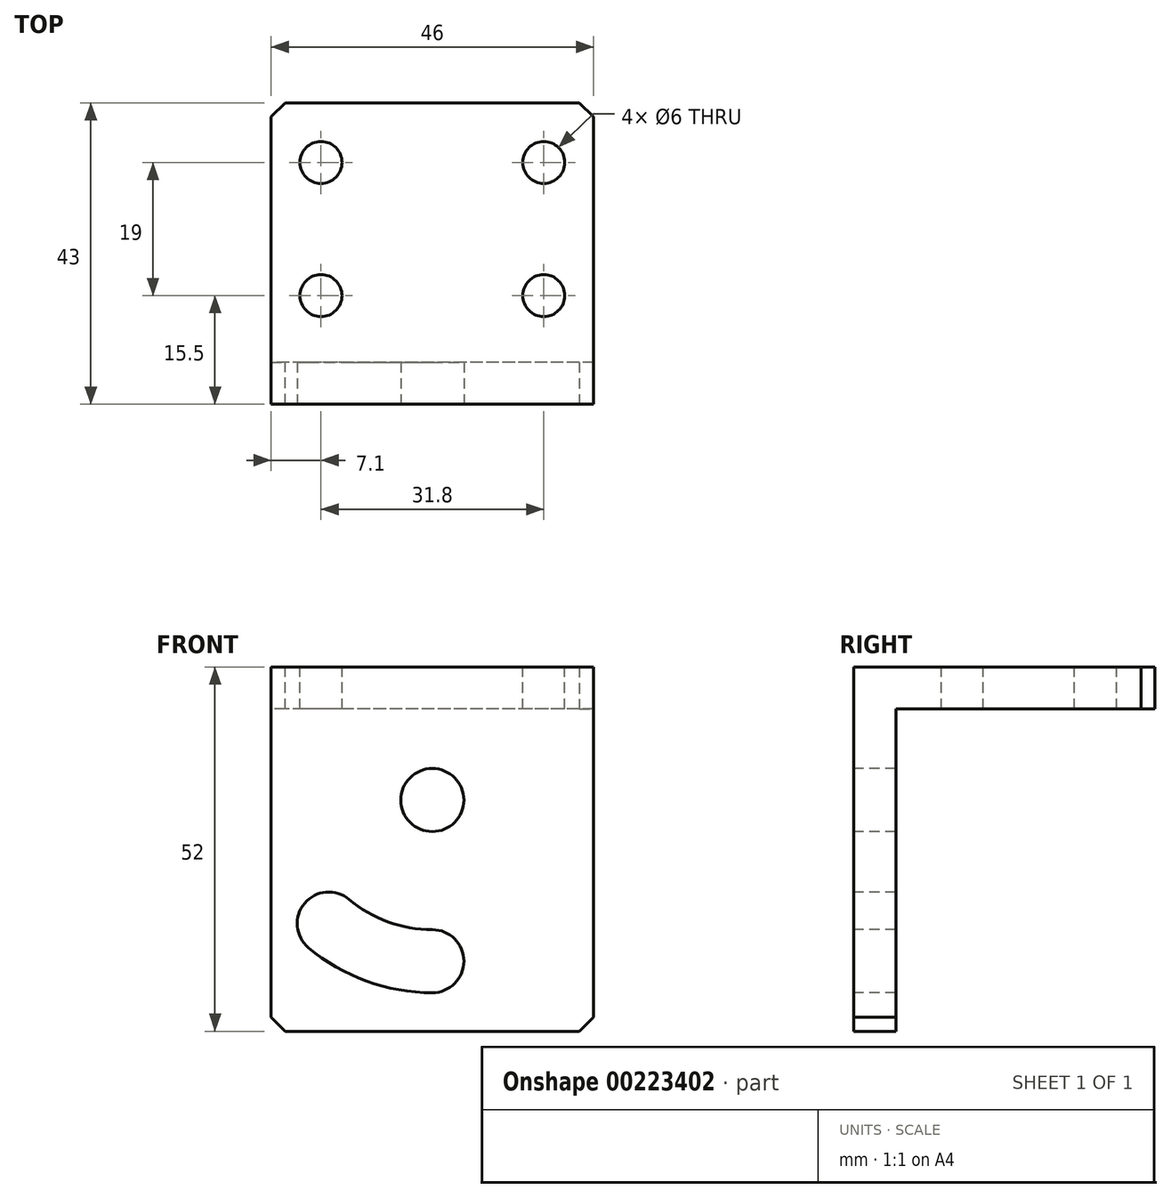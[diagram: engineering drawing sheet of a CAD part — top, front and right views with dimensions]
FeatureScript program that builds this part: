
annotation { "Feature Type Name" : "Feature", "Feature Type Description" : "" }
export const myFeature = defineFeature(function(context is Context, id is Id, definition is map)
    precondition{}
    {
        {
            var Q0;
            Q0=qCreatedBy(makeId("Right.planeOp"),FACE);
            var sketch = newSketch(context, id + "F0", { "sketchPlane" : qUnion([Q0])});
            skLineSegment(sketch, "E0", {"start": v(0, 0) * mm, "end": v(0, -52) * mm});
            skLineSegment(sketch, "E1", {"start": v(0, -52) * mm, "end": v(6, -52) * mm});
            skLineSegment(sketch, "E2", {"start": v(6, -52) * mm, "end": v(6, -6) * mm});
            skLineSegment(sketch, "E3", {"start": v(6, -6) * mm, "end": v(43, -6) * mm});
            skLineSegment(sketch, "E4", {"start": v(43, -6) * mm, "end": v(43, 0) * mm});
            skLineSegment(sketch, "E5", {"start": v(43, 0) * mm, "end": v(0, 0) * mm});
            skSolve(sketch);
        }
        {
            var Q0;
            Q0 = qSketchRegion(id + "F0", true);
            extrude(context, id + "F1", {"entities" : qUnion([Q0]), "depth" : 46 * mm});
        }
        {
            var Q0;
            Q0=qCreatedBy(makeId("Top.planeOp"),FACE);
            var sketch = newSketch(context, id + "F2", { "sketchPlane" : qUnion([Q0])});
            skLineSegment(sketch, "E6", {"start": v(23, -4.49) * mm, "end": v(23, 57.42) * mm});
            skCircle(sketch, "E7", {"center": v(38.9, 15.5) * mm, "radius": 3 * mm});
            skCircle(sketch, "E8", {"center": v(38.9, 34.5) * mm, "radius": 3 * mm});
            skCircle(sketch, "E9.MirrorC", {"center": v(7.1, 15.5) * mm, "radius": 3 * mm});
            skCircle(sketch, "E10.MirrorC", {"center": v(7.1, 34.5) * mm, "radius": 3 * mm});
            skSolve(sketch);
        }
        {
            var Q0;
            Q0 = qSketchRegion(id + "F2", true);
            extrude(context, id + "F3", {"entities" : qUnion([Q0]), "operationType" : NewBodyOperationType.REMOVE, "oppositeDirection" : true, "depth" : 25 * mm});
        }
        {
            var Q0;
            Q0=makeQuery(id+"F1.opExtrude","SWEPT_FACE",FACE,{"disambiguationData":[OSD([sQuery(id+"F0.wireOp",EDGE,"E0")])]});
            var sketch = newSketch(context, id + "F4", { "sketchPlane" : qUnion([Q0])});
            skCircle(sketch, "E11", {"center": v(23, -19) * mm, "radius": 4.5 * mm});
            skArc(sketch, "E12", {"start": v(11.1, -33.17) * mm, "mid": v(16.67, -36.38) * mm, "end": v(23, -37.5) * mm});
            skArc(sketch, "E13", {"start": v(5.32, -40.07) * mm, "mid": v(13.6, -44.84) * mm, "end": v(23, -46.5) * mm});
            skArc(sketch, "E14", {"start": v(23, -46.5) * mm, "mid": v(27.5, -42) * mm, "end": v(23, -37.5) * mm});
            skArc(sketch, "E15", {"start": v(11.1, -33.17) * mm, "mid": v(4.77, -33.73) * mm, "end": v(5.32, -40.07) * mm});
            skSolve(sketch);
        }
        {
            var Q0;
            Q0 = qSketchRegion(id + "F4", true);
            extrude(context, id + "F5", {"entities" : qUnion([Q0]), "operationType" : NewBodyOperationType.REMOVE, "oppositeDirection" : true, "depth" : 25 * mm});
        }
        {
            var Q0;
            Q0=makeQuery(id+"F1.opExtrude","CAP_EDGE",EDGE,{"disambiguationData":[OSD([sQuery(id+"F0.wireOp",EDGE,"E4")])],"isStart":true});
            var Q1;
            Q1=makeQuery(id+"F1.opExtrude","CAP_EDGE",EDGE,{"disambiguationData":[OSD([sQuery(id+"F0.wireOp",EDGE,"E4")])],"isStart":false});
            var Q2;
            Q2=makeQuery(id+"F1.opExtrude","CAP_EDGE",EDGE,{"disambiguationData":[OSD([sQuery(id+"F0.wireOp",EDGE,"E1")])],"isStart":false});
            var Q3;
            Q3=makeQuery(id+"F1.opExtrude","CAP_EDGE",EDGE,{"disambiguationData":[OSD([sQuery(id+"F0.wireOp",EDGE,"E1")])],"isStart":true});
            chamfer(context, id + "F6", {"entities" : qUnion([Q0, Q1, Q2, Q3]), "width" : 2 * mm, "tangentPropagation" : true});
        }
    });
